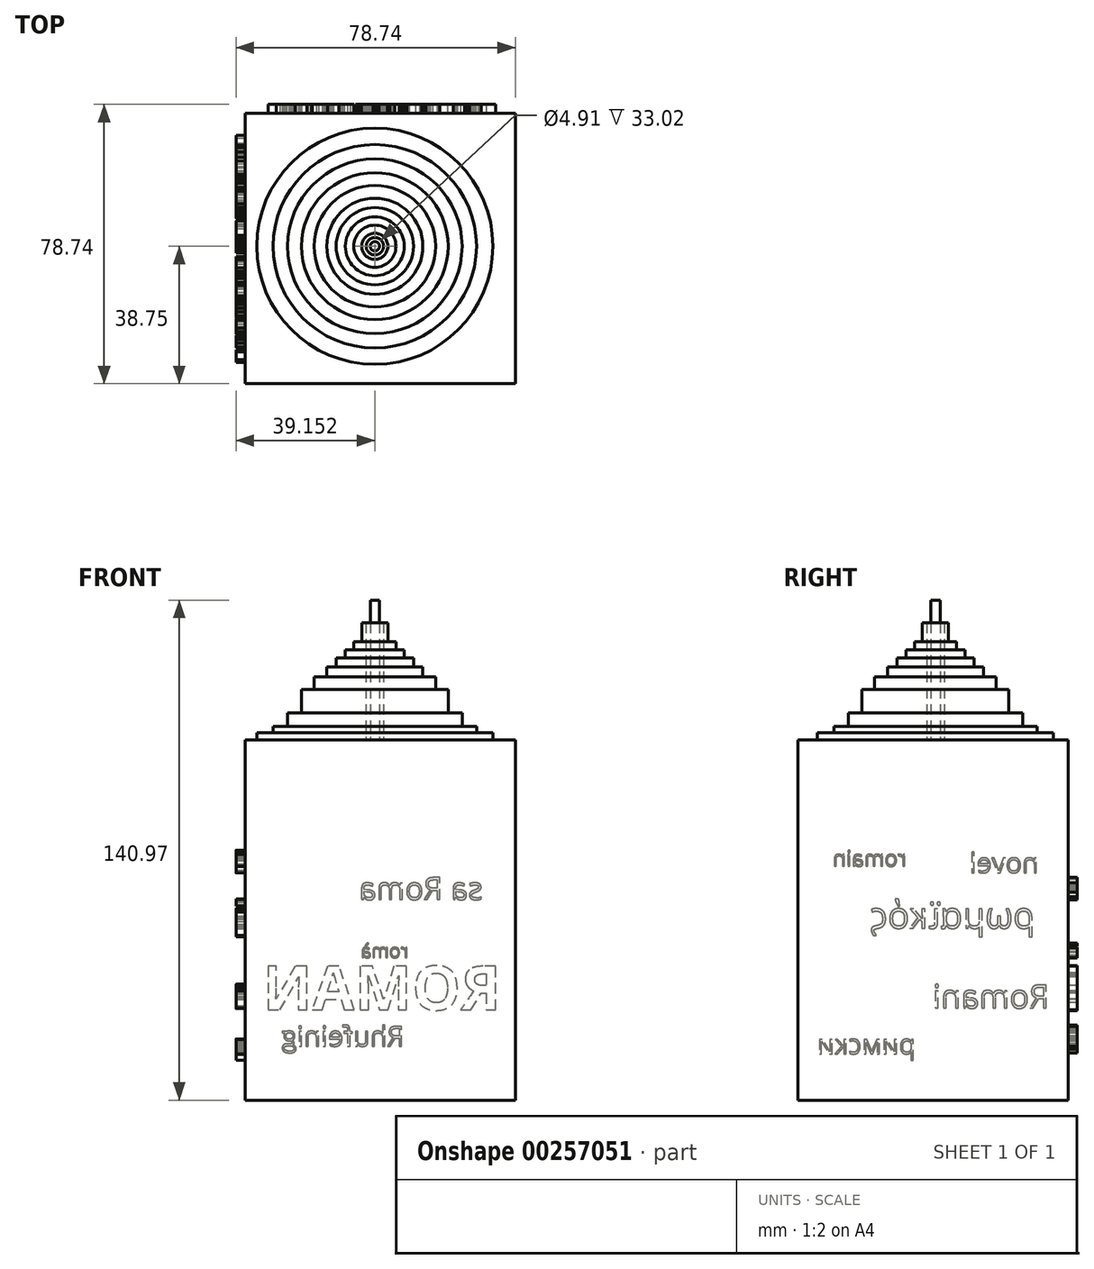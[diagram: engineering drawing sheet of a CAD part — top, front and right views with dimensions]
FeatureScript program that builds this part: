
annotation { "Feature Type Name" : "Feature", "Feature Type Description" : "" }
export const myFeature = defineFeature(function(context is Context, id is Id, definition is map)
    precondition{}
    {
        {
            var Q0;
            Q0=qCreatedBy(makeId("Top.planeOp"),FACE);
            var sketch = newSketch(context, id + "F0", { "sketchPlane" : qUnion([Q0])});
            skLineSegment(sketch, "E0.bottom", {"start": v(-114.86, 51.41) * mm, "end": v(-38.66, 51.41) * mm});
            skLineSegment(sketch, "E0.top", {"start": v(-114.86, -24.79) * mm, "end": v(-38.66, -24.79) * mm});
            skLineSegment(sketch, "E0.left", {"start": v(-114.86, 51.41) * mm, "end": v(-114.86, -24.79) * mm});
            skLineSegment(sketch, "E0.right", {"start": v(-38.66, 51.41) * mm, "end": v(-38.66, -24.79) * mm});
            skSolve(sketch);
        }
        {
            var Q0;
            Q0 = qSketchRegion(id + "F0", true);
            extrude(context, id + "F1", {"entities" : qUnion([Q0]), "depth" : 76.2 * mm});
        }
        {
            var Q0;
            Q0=makeQuery(id+"F1.opExtrude","SWEPT_FACE",FACE,{"disambiguationData":[OSD([sQuery(id+"F0.wireOp",EDGE,"E0.left")])]});
            var sketch = newSketch(context, id + "F2", { "sketchPlane" : qUnion([Q0])});
            skText(sketch, "E1", { "text": "novel\n", "fontName": "OpenSans-Regular.ttf"});
            skText(sketch, "E2", { "text": "ρωμαϊκός", "fontName": "OpenSans-Regular.ttf"});
            skText(sketch, "E3", { "text": "Romani", "fontName": "OpenSans-Regular.ttf"});
            skText(sketch, "E4", { "text": "римски", "fontName": "OpenSans-Regular.ttf"});
            skText(sketch, "E5", { "text": "romain", "fontName": "OpenSans-Regular.ttf"});
            const initialGuessF2  = {"E1": [-0.04308, 0.06413, 1, 0, 0.00554], "E2": [-0.042, 0.04846, 1, 0, 0.00735], "E3": [-0.04609, 0.02593, 1, 0, 0.00663], "E4": [-0.00837, 0.01304, 1, 0, 0.00554], "E5": [-0.00584, 0.06593, 1, 0, 0.00446]};
            skSetInitialGuess(sketch, initialGuessF2);
            skSolve(sketch);
        }
        {
            var Q0;
            Q0 = qSketchRegion(id + "F2", true);
            extrude(context, id + "F3", {"entities" : qUnion([Q0]), "operationType" : NewBodyOperationType.ADD, "depth" : 2.54 * mm});
        }
        {
            var Q0;
            Q0=makeQuery(id+"F1.opExtrude","SWEPT_FACE",FACE,{"disambiguationData":[OSD([sQuery(id+"F0.wireOp",EDGE,"E0.bottom")])]});
            var sketch = newSketch(context, id + "F4", { "sketchPlane" : qUnion([Q0])});
            skText(sketch, "E6", { "text": "sa Roma", "fontName": "OpenSans-Regular.ttf"});
            skText(sketch, "E7", { "text": "romà", "fontName": "OpenSans-Regular.ttf"});
            skText(sketch, "E8", { "text": "Rhufeinig", "fontName": "OpenSans-Regular.ttf"});
            skText(sketch, "E9", { "text": "ROMAN", "fontName": "OpenSans-Bold.ttf"});
            const initialGuessF4  = {"E6": [0.04784, 0.05654, 1, 0, 0.00627], "E7": [0.0688, 0.04015, 1, 0, 0.00386], "E8": [0.0699, 0.0152, 1, 0, 0.00566], "E9": [0.04266, 0.02545, 1, 0, 0.01241]};
            skSetInitialGuess(sketch, initialGuessF4);
            skSolve(sketch);
        }
        {
            var Q0;
            Q0 = qSketchRegion(id + "F4", true);
            extrude(context, id + "F5", {"entities" : qUnion([Q0]), "operationType" : NewBodyOperationType.ADD, "depth" : 2.54 * mm});
        }
        {
            var Q0;
            Q0=makeQuery(id+"F1.opExtrude","CAP_FACE",FACE,{"disambiguationData":[OSD([sQuery(id+"F0.wireOp",EDGE,"E0.bottom"),sQuery(id+"F0.wireOp",EDGE,"E0.top"),sQuery(id+"F0.wireOp",EDGE,"E0.left"),sQuery(id+"F0.wireOp",EDGE,"E0.right")])],"isStart":false});
            extrude(context, id + "F6", {"entities" : qUnion([Q0]), "operationType" : NewBodyOperationType.ADD, "depth" : 25.4 * mm});
        }
        {
            var Q0;
            Q0=makeQuery(id+"F6.opExtrude","CAP_FACE",FACE,{"disambiguationData":[OSD([sQuery(id+"F0.wireOp",EDGE,"E0.bottom"),sQuery(id+"F0.wireOp",EDGE,"E0.top"),sQuery(id+"F0.wireOp",EDGE,"E0.left"),sQuery(id+"F0.wireOp",EDGE,"E0.right")])],"isStart":false});
            var sketch = newSketch(context, id + "F7", { "sketchPlane" : qUnion([Q0])});
            skCircle(sketch, "E10", {"center": v(-78.25, 13.96) * mm, "radius": 33.28 * mm});
            skCircle(sketch, "E11", {"center": v(-78.25, 13.96) * mm, "radius": 28.66 * mm});
            skCircle(sketch, "E12", {"center": v(-78.25, 13.96) * mm, "radius": 24.6 * mm});
            skCircle(sketch, "E13", {"center": v(-78.25, 13.96) * mm, "radius": 20.7 * mm});
            skCircle(sketch, "E14", {"center": v(-78.25, 13.96) * mm, "radius": 17.13 * mm});
            skCircle(sketch, "E15", {"center": v(-78.25, 13.96) * mm, "radius": 13.53 * mm});
            skCircle(sketch, "E16", {"center": v(-78.25, 13.96) * mm, "radius": 10.9 * mm});
            skCircle(sketch, "E17", {"center": v(-78.25, 13.96) * mm, "radius": 8.3 * mm});
            skCircle(sketch, "E18", {"center": v(-78.25, 13.96) * mm, "radius": 5.95 * mm});
            skCircle(sketch, "E19", {"center": v(-78.25, 13.96) * mm, "radius": 3.68 * mm});
            skCircle(sketch, "E20", {"center": v(-78.25, 13.96) * mm, "radius": 2.45 * mm});
            skCircle(sketch, "E21", {"center": v(-78.25, 13.96) * mm, "radius": 1.3 * mm});
            skSolve(sketch);
        }
        {
            var Q0;
            Q0=makeQuery(id+"F7.imprint","IMPRINT",FACE,{"disambiguationData":[TD([[makeQuery(id+"F7.imprint","IMPRINT",EDGE,{"derivedFrom":sQuery(id+"F7.wireOp",EDGE,"E21")}),1.0]])]});
            extrude(context, id + "F8", {"entities" : qUnion([Q0]), "operationType" : NewBodyOperationType.ADD, "depth" : 39.37 * mm});
        }
        {
            var Q0;
            Q0=makeQuery(id+"F7.imprint","IMPRINT",FACE,{"disambiguationData":[TD([[makeQuery(id+"F7.imprint","IMPRINT",EDGE,{"derivedFrom":sQuery(id+"F7.wireOp",EDGE,"E19")}),1.0]])]});
            extrude(context, id + "F9", {"entities" : qUnion([Q0]), "operationType" : NewBodyOperationType.ADD, "depth" : 33.02 * mm});
        }
        {
            var Q0;
            Q0=makeQuery(id+"F7.imprint","IMPRINT",FACE,{"disambiguationData":[TD([[makeQuery(id+"F7.imprint","IMPRINT",EDGE,{"derivedFrom":sQuery(id+"F7.wireOp",EDGE,"E18")}),1.0]])]});
            extrude(context, id + "F10", {"entities" : qUnion([Q0]), "operationType" : NewBodyOperationType.ADD, "depth" : 27.7 * mm});
        }
        {
            var Q0;
            Q0=makeQuery(id+"F7.imprint","IMPRINT",FACE,{"disambiguationData":[TD([[makeQuery(id+"F7.imprint","IMPRINT",EDGE,{"derivedFrom":sQuery(id+"F7.wireOp",EDGE,"E17")}),1.0]])]});
            extrude(context, id + "F11", {"entities" : qUnion([Q0]), "operationType" : NewBodyOperationType.ADD, "depth" : 25.4 * mm});
        }
        {
            var Q0;
            Q0=makeQuery(id+"F7.imprint","IMPRINT",FACE,{"disambiguationData":[TD([[makeQuery(id+"F7.imprint","IMPRINT",EDGE,{"derivedFrom":sQuery(id+"F7.wireOp",EDGE,"E16")}),1.0]])]});
            extrude(context, id + "F12", {"entities" : qUnion([Q0]), "operationType" : NewBodyOperationType.ADD, "depth" : 23.1 * mm});
        }
        {
            var Q0;
            Q0=makeQuery(id+"F7.imprint","IMPRINT",FACE,{"disambiguationData":[TD([[makeQuery(id+"F7.imprint","IMPRINT",EDGE,{"derivedFrom":sQuery(id+"F7.wireOp",EDGE,"E15")}),1.0]])]});
            extrude(context, id + "F13", {"entities" : qUnion([Q0]), "operationType" : NewBodyOperationType.ADD, "depth" : 20.57 * mm});
        }
        {
            var Q0;
            Q0=makeQuery(id+"F7.imprint","IMPRINT",FACE,{"disambiguationData":[TD([[makeQuery(id+"F7.imprint","IMPRINT",EDGE,{"derivedFrom":sQuery(id+"F7.wireOp",EDGE,"E14")}),1.0]])]});
            extrude(context, id + "F14", {"entities" : qUnion([Q0]), "operationType" : NewBodyOperationType.ADD, "depth" : 17.78 * mm});
        }
        {
            var Q0;
            Q0=makeQuery(id+"F7.imprint","IMPRINT",FACE,{"disambiguationData":[TD([[makeQuery(id+"F7.imprint","IMPRINT",EDGE,{"derivedFrom":sQuery(id+"F7.wireOp",EDGE,"E13")}),1.0]])]});
            extrude(context, id + "F15", {"entities" : qUnion([Q0]), "operationType" : NewBodyOperationType.ADD, "depth" : 14.22 * mm});
        }
        {
            var Q0;
            Q0=makeQuery(id+"F7.imprint","IMPRINT",FACE,{"disambiguationData":[TD([[makeQuery(id+"F7.imprint","IMPRINT",EDGE,{"derivedFrom":sQuery(id+"F7.wireOp",EDGE,"E12")}),1.0]])]});
            extrude(context, id + "F16", {"entities" : qUnion([Q0]), "operationType" : NewBodyOperationType.ADD, "depth" : 7.62 * mm});
        }
        {
            var Q0;
            Q0=makeQuery(id+"F7.imprint","IMPRINT",FACE,{"disambiguationData":[TD([[makeQuery(id+"F7.imprint","IMPRINT",EDGE,{"derivedFrom":sQuery(id+"F7.wireOp",EDGE,"E11")}),1.0]])]});
            extrude(context, id + "F17", {"entities" : qUnion([Q0]), "operationType" : NewBodyOperationType.ADD, "depth" : 3.8 * mm});
        }
        {
            var Q0;
            Q0=makeQuery(id+"F7.imprint","IMPRINT",FACE,{"disambiguationData":[TD([[makeQuery(id+"F7.imprint","IMPRINT",EDGE,{"derivedFrom":sQuery(id+"F7.wireOp",EDGE,"E10")}),1.0]])]});
            extrude(context, id + "F18", {"entities" : qUnion([Q0]), "operationType" : NewBodyOperationType.ADD, "depth" : 2.03 * mm});
        }
    });
